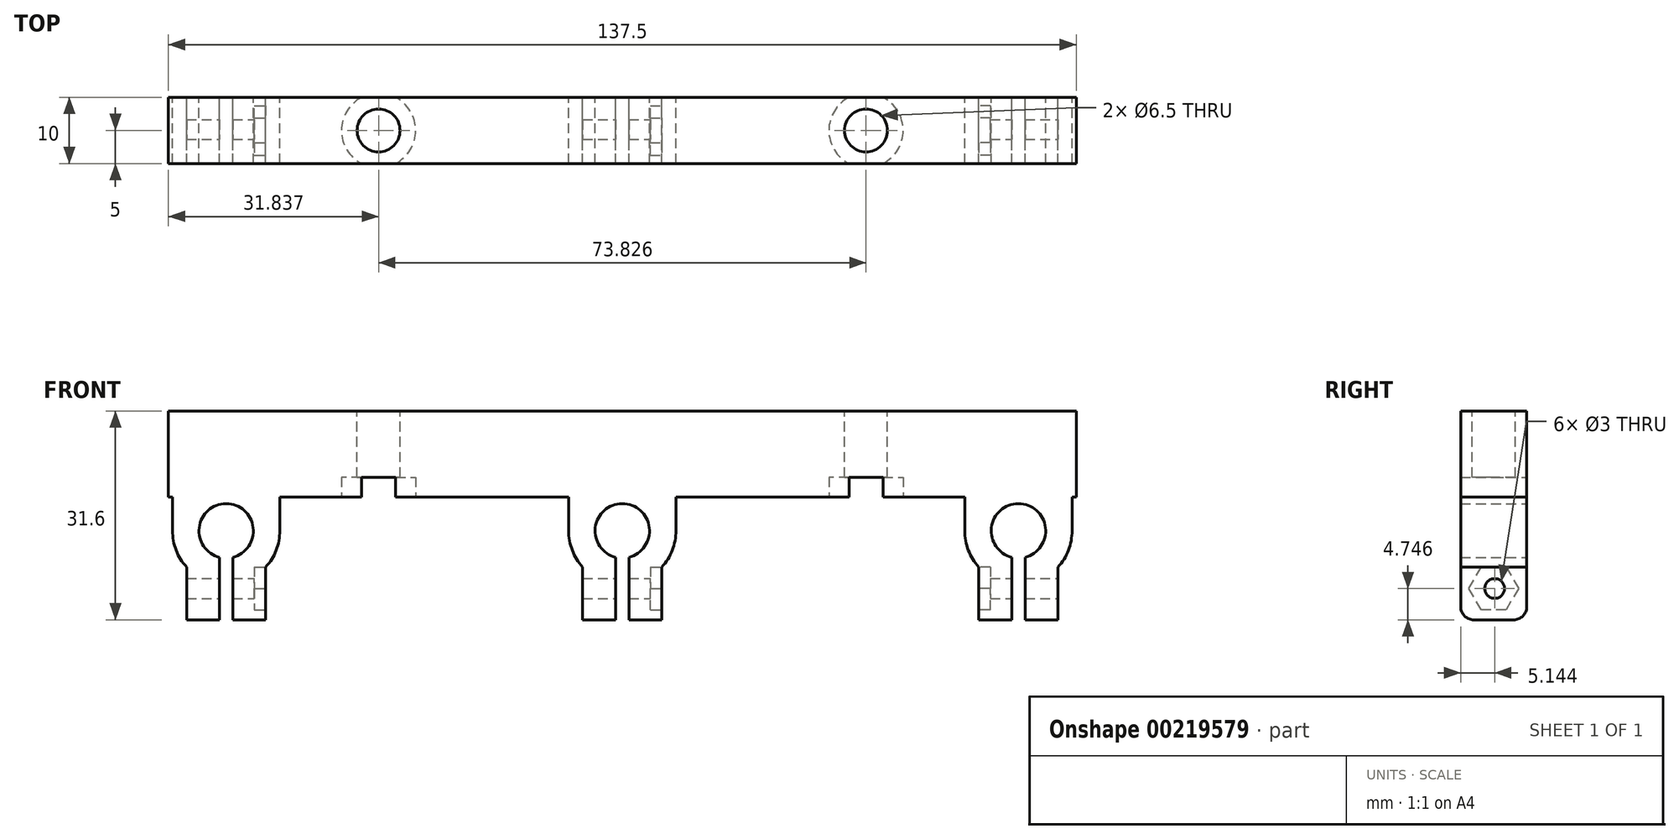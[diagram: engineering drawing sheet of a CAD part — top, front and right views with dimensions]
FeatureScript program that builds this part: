
annotation { "Feature Type Name" : "Feature", "Feature Type Description" : "" }
export const myFeature = defineFeature(function(context is Context, id is Id, definition is map)
    precondition{}
    {
        {
            var Q0;
            Q0=qCreatedBy(makeId("Top.planeOp"),FACE);
            var sketch = newSketch(context, id + "F0", { "sketchPlane" : qUnion([Q0])});
            skLineSegment(sketch, "E0.bottom", {"start": v(68.75, -5) * mm, "end": v(-68.75, -5) * mm});
            skLineSegment(sketch, "E0.top", {"start": v(68.75, 5) * mm, "end": v(-68.75, 5) * mm});
            skLineSegment(sketch, "E0.left", {"start": v(68.75, -5) * mm, "end": v(68.75, 5) * mm});
            skLineSegment(sketch, "E0.right", {"start": v(-68.75, -5) * mm, "end": v(-68.75, 5) * mm});
            skPoint(sketch, "E0.middle", {"position": v(0, 0) * mm});
            skSolve(sketch);
        }
        {
            var Q0;
            Q0 = qSketchRegion(id + "F0", true);
            extrude(context, id + "F1", {"entities" : qUnion([Q0]), "depth" : 9 * mm});
        }
        {
            var Q0;
            Q0=makeQuery(id+"F1.opExtrude","SWEPT_FACE",FACE,{"disambiguationData":[OSD([sQuery(id+"F0.wireOp",EDGE,"E0.top")])]});
            var sketch = newSketch(context, id + "F2", { "sketchPlane" : qUnion([Q0])});
            skCircle(sketch, "E1", {"center": v(0, -9.13) * mm, "radius": 4.12 * mm});
            skPoint(sketch, "E1.centerSnap0", {"position": v(0, 0) * mm});
            skCircle(sketch, "E2", {"center": v(-60, -9.12) * mm, "radius": 4.12 * mm});
            skCircle(sketch, "E3", {"center": v(60, -9.13) * mm, "radius": 4.12 * mm});
            skLineSegment(sketch, "E4", {"start": v(60, -9.13) * mm, "end": v(0, -9.13) * mm, "construction": true});
            skLineSegment(sketch, "E5", {"start": v(-60, -9.12) * mm, "end": v(0, -9.13) * mm, "construction": true});
            skArc(sketch, "E6", {"start": v(-68.12, -9.12) * mm, "mid": v(-60, -17.25) * mm, "end": v(-51.88, -9.12) * mm});
            skLineSegment(sketch, "E7", {"start": v(-68.12, -9.12) * mm, "end": v(-51.88, -9.12) * mm, "construction": true});
            skArc(sketch, "E8", {"start": v(-8.12, -9.13) * mm, "mid": v(0, -17.25) * mm, "end": v(8.12, -9.13) * mm});
            skLineSegment(sketch, "E9", {"start": v(-8.12, -9.12) * mm, "end": v(8.12, -9.13) * mm, "construction": true});
            skArc(sketch, "E10", {"start": v(51.88, -9.13) * mm, "mid": v(60, -17.25) * mm, "end": v(68.12, -9.13) * mm});
            skLineSegment(sketch, "E11", {"start": v(51.88, -9.13) * mm, "end": v(68.12, -9.13) * mm, "construction": true});
            skLineSegment(sketch, "E12", {"start": v(-68.12, -9.12) * mm, "end": v(-68.12, -4) * mm});
            skLineSegment(sketch, "E13", {"start": v(-51.88, -9.12) * mm, "end": v(-51.88, -4) * mm});
            skLineSegment(sketch, "E14", {"start": v(-8.12, -9.13) * mm, "end": v(-8.12, -4) * mm});
            skLineSegment(sketch, "E15", {"start": v(8.12, -9.13) * mm, "end": v(8.12, -4) * mm});
            skLineSegment(sketch, "E16", {"start": v(51.88, -9.13) * mm, "end": v(51.88, -4) * mm});
            skLineSegment(sketch, "E17", {"start": v(68.12, -9.13) * mm, "end": v(68.12, -4) * mm});
            skLineSegment(sketch, "E18", {"start": v(68.12, -4) * mm, "end": v(68.75, -4) * mm});
            skLineSegment(sketch, "E19", {"start": v(68.75, -4) * mm, "end": v(68.75, 0) * mm});
            skLineSegment(sketch, "E20", {"start": v(51.88, -4) * mm, "end": v(8.12, -4) * mm});
            skLineSegment(sketch, "E21", {"start": v(-8.12, -4) * mm, "end": v(-51.88, -4) * mm});
            skLineSegment(sketch, "E22", {"start": v(-68.12, -4) * mm, "end": v(-68.75, -4) * mm});
            skLineSegment(sketch, "E23", {"start": v(-68.75, -4) * mm, "end": v(-68.75, 0) * mm});
            skLineSegment(sketch, "E24.bottom", {"start": v(66, -14.6) * mm, "end": v(54, -14.6) * mm, "construction": true});
            skLineSegment(sketch, "E24.top", {"start": v(66, -22.6) * mm, "end": v(54, -22.6) * mm});
            skLineSegment(sketch, "E24.left", {"start": v(66, -14.6) * mm, "end": v(66, -22.6) * mm});
            skLineSegment(sketch, "E24.right", {"start": v(54, -14.6) * mm, "end": v(54, -22.6) * mm});
            skLineSegment(sketch, "E25.bottom", {"start": v(6, -14.6) * mm, "end": v(-6, -14.6) * mm, "construction": true});
            skLineSegment(sketch, "E25.top", {"start": v(6, -22.6) * mm, "end": v(-6, -22.6) * mm});
            skLineSegment(sketch, "E25.left", {"start": v(6, -14.6) * mm, "end": v(6, -22.6) * mm});
            skLineSegment(sketch, "E25.right", {"start": v(-6, -14.6) * mm, "end": v(-6, -22.6) * mm});
            skLineSegment(sketch, "E26.bottom", {"start": v(-54, -14.6) * mm, "end": v(-66, -14.6) * mm, "construction": true});
            skLineSegment(sketch, "E26.top", {"start": v(-54, -22.6) * mm, "end": v(-66, -22.6) * mm});
            skLineSegment(sketch, "E26.left", {"start": v(-54, -14.6) * mm, "end": v(-54, -22.6) * mm});
            skLineSegment(sketch, "E26.right", {"start": v(-66, -14.6) * mm, "end": v(-66, -22.6) * mm});
            skLineSegment(sketch, "E27.bottom", {"start": v(61, -13.13) * mm, "end": v(59, -13.13) * mm});
            skLineSegment(sketch, "E27.top", {"start": v(61, -22.6) * mm, "end": v(59, -22.6) * mm});
            skLineSegment(sketch, "E27.left", {"start": v(61, -13.13) * mm, "end": v(61, -22.6) * mm});
            skLineSegment(sketch, "E27.right", {"start": v(59, -13.13) * mm, "end": v(59, -22.6) * mm});
            skLineSegment(sketch, "E28.bottom", {"start": v(1, -13.13) * mm, "end": v(-1, -13.13) * mm});
            skLineSegment(sketch, "E28.top", {"start": v(1, -22.6) * mm, "end": v(-1, -22.6) * mm});
            skLineSegment(sketch, "E28.left", {"start": v(1, -13.13) * mm, "end": v(1, -22.6) * mm});
            skLineSegment(sketch, "E28.right", {"start": v(-1, -13.13) * mm, "end": v(-1, -22.6) * mm});
            skLineSegment(sketch, "E29.bottom", {"start": v(-59, -13.13) * mm, "end": v(-61, -13.13) * mm});
            skLineSegment(sketch, "E29.top", {"start": v(-59, -22.6) * mm, "end": v(-61, -22.6) * mm});
            skLineSegment(sketch, "E29.left", {"start": v(-59, -13.13) * mm, "end": v(-59, -22.6) * mm});
            skLineSegment(sketch, "E29.right", {"start": v(-61, -13.13) * mm, "end": v(-61, -22.6) * mm});
            skSolve(sketch);
        }
        {
            var Q0;
            {var subQ0=sQuery(id+"F2.wireOp",EDGE,"E26.right");Q0=makeQuery(id+"F2.imprint","IMPRINT",FACE,{"disambiguationData":[TD([[makeQuery(id+"F2.imprint","IMPRINT",EDGE,{"derivedFrom":subQ0}),1.0]])]});}
            var Q1;
            {var subQ0=sQuery(id+"F2.wireOp",EDGE,"E26.left");Q1=makeQuery(id+"F2.imprint","IMPRINT",FACE,{"disambiguationData":[TD([[makeQuery(id+"F2.imprint","IMPRINT",EDGE,{"derivedFrom":subQ0}),-1.0]])]});}
            var Q2;
            {var subQ0=sQuery(id+"F2.wireOp",EDGE,"E25.right");Q2=makeQuery(id+"F2.imprint","IMPRINT",FACE,{"disambiguationData":[TD([[makeQuery(id+"F2.imprint","IMPRINT",EDGE,{"derivedFrom":subQ0}),1.0]])]});}
            var Q3;
            {var subQ0=sQuery(id+"F2.wireOp",EDGE,"E25.left");Q3=makeQuery(id+"F2.imprint","IMPRINT",FACE,{"disambiguationData":[TD([[makeQuery(id+"F2.imprint","IMPRINT",EDGE,{"derivedFrom":subQ0}),-1.0]])]});}
            var Q4;
            {var subQ0=sQuery(id+"F2.wireOp",EDGE,"E24.right");Q4=makeQuery(id+"F2.imprint","IMPRINT",FACE,{"disambiguationData":[TD([[makeQuery(id+"F2.imprint","IMPRINT",EDGE,{"derivedFrom":subQ0}),1.0]])]});}
            var Q5;
            {var subQ0=sQuery(id+"F2.wireOp",EDGE,"E24.left");Q5=makeQuery(id+"F2.imprint","IMPRINT",FACE,{"disambiguationData":[TD([[makeQuery(id+"F2.imprint","IMPRINT",EDGE,{"derivedFrom":subQ0}),-1.0]])]});}
            var Q6;
            {var subQ3=sQuery(id+"F2.wireOp",EDGE,"E12");Q6=makeQuery(id+"F2.imprint","IMPRINT",FACE,{"disambiguationData":[TD([[makeQuery(id+"F2.imprint","IMPRINT",EDGE,{"derivedFrom":subQ3}),-1.0]])]});}
            var Q7;
            Q7=makeQuery(id+"F1.opExtrude","SWEPT_FACE",FACE,{"disambiguationData":[OSD([sQuery(id+"F0.wireOp",EDGE,"E0.bottom")])]});
            extrude(context, id + "F3", {"entities" : qUnion([Q0, Q1, Q2, Q3, Q4, Q5, Q6]), "operationType" : NewBodyOperationType.ADD, "endBound" : BoundingType.UP_TO_SURFACE, "oppositeDirection" : true, "endBoundEntityFace" : qUnion([Q7]), "depth" : 10 * mm});
        }
        {
            var Q0;
            Q0=makeQuery(id+"F3.opExtrude","SWEPT_FACE",FACE,{"disambiguationData":[OSD([sQuery(id+"F2.wireOp",EDGE,"E26.left")])]});
            var sketch = newSketch(context, id + "F4", { "sketchPlane" : qUnion([Q0])});
            skCircle(sketch, "E30.cCircle", {"center": v(0, -17.85) * mm, "radius": 3.25 * mm, "construction": true});
            skPoint(sketch, "E30.cCircle.centerSnap1", {"position": v(0, -14.6) * mm});
            skLineSegment(sketch, "E30.0", {"start": v(1.88, -14.6) * mm, "end": v(3.75, -17.85) * mm});
            skLineSegment(sketch, "E30.1", {"start": v(3.75, -17.85) * mm, "end": v(1.88, -21.1) * mm});
            skLineSegment(sketch, "E30.2", {"start": v(1.88, -21.1) * mm, "end": v(-1.88, -21.1) * mm});
            skLineSegment(sketch, "E30.3", {"start": v(-1.88, -21.1) * mm, "end": v(-3.75, -17.85) * mm});
            skLineSegment(sketch, "E30.4", {"start": v(-3.75, -17.85) * mm, "end": v(-1.88, -14.6) * mm});
            skLineSegment(sketch, "E30.5", {"start": v(-1.88, -14.6) * mm, "end": v(1.88, -14.6) * mm});
            skPoint(sketch, "E30.0.midPoint", {"position": v(2.81, -16.23) * mm});
            skLineSegment(sketch, "E31.0", {"start": v(5, -14.6) * mm, "end": v(-5, -14.6) * mm});
            skSolve(sketch);
        }
        {
            var Q0;
            Q0 = qSketchRegion(id + "F4", true);
            extrude(context, id + "F5", {"entities" : qUnion([Q0]), "operationType" : NewBodyOperationType.REMOVE, "oppositeDirection" : true, "depth" : 1.75 * mm});
        }
        {
            var Q0;
            Q0=makeQuery(id+"F3.opExtrude","SWEPT_FACE",FACE,{"disambiguationData":[OSD([sQuery(id+"F2.wireOp",EDGE,"E25.right")])]});
            var sketch = newSketch(context, id + "F6", { "sketchPlane" : qUnion([Q0])});
            skLineSegment(sketch, "E32.0.0", {"start": v(1.88, -14.6) * mm, "end": v(3.75, -17.85) * mm});
            skLineSegment(sketch, "E32.0.1", {"start": v(3.75, -17.85) * mm, "end": v(1.88, -21.1) * mm});
            skLineSegment(sketch, "E32.0.2", {"start": v(1.88, -21.1) * mm, "end": v(-1.88, -21.1) * mm});
            skLineSegment(sketch, "E32.0.3", {"start": v(-1.88, -21.1) * mm, "end": v(-3.75, -17.85) * mm});
            skLineSegment(sketch, "E32.0.4", {"start": v(-3.75, -17.85) * mm, "end": v(-1.88, -14.6) * mm});
            skLineSegment(sketch, "E32.0.5", {"start": v(-1.88, -14.6) * mm, "end": v(1.88, -14.6) * mm});
            skSolve(sketch);
        }
        {
            var Q0;
            Q0 = qSketchRegion(id + "F6", true);
            extrude(context, id + "F7", {"entities" : qUnion([Q0]), "operationType" : NewBodyOperationType.REMOVE, "oppositeDirection" : true, "depth" : 1.75 * mm});
        }
        {
            var Q0;
            Q0=makeQuery(id+"F3.opExtrude","SWEPT_FACE",FACE,{"disambiguationData":[OSD([sQuery(id+"F2.wireOp",EDGE,"E24.right")])]});
            var sketch = newSketch(context, id + "F8", { "sketchPlane" : qUnion([Q0])});
            skLineSegment(sketch, "E33.0.0", {"start": v(-1.88, -14.6) * mm, "end": v(-3.75, -17.85) * mm});
            skLineSegment(sketch, "E33.0.1", {"start": v(-3.75, -17.85) * mm, "end": v(-1.88, -21.1) * mm});
            skLineSegment(sketch, "E33.0.2", {"start": v(-1.88, -21.1) * mm, "end": v(1.88, -21.1) * mm});
            skLineSegment(sketch, "E33.0.3", {"start": v(1.88, -21.1) * mm, "end": v(3.75, -17.85) * mm});
            skLineSegment(sketch, "E33.0.4", {"start": v(3.75, -17.85) * mm, "end": v(1.88, -14.6) * mm});
            skLineSegment(sketch, "E33.0.5", {"start": v(1.88, -14.6) * mm, "end": v(-1.88, -14.6) * mm});
            skSolve(sketch);
        }
        {
            var Q0;
            Q0 = qSketchRegion(id + "F8", true);
            extrude(context, id + "F9", {"entities" : qUnion([Q0]), "operationType" : NewBodyOperationType.REMOVE, "oppositeDirection" : true, "depth" : 1.75 * mm});
        }
        {
            var Q0;
            Q0=makeQuery(id+"F3.opExtrude","SWEPT_FACE",FACE,{"disambiguationData":[OSD([sQuery(id+"F2.wireOp",EDGE,"E26.right")])]});
            var sketch = newSketch(context, id + "F10", { "sketchPlane" : qUnion([Q0])});
            skCircle(sketch, "E34", {"center": v(0.14, -17.85) * mm, "radius": 1.5 * mm});
            skPoint(sketch, "E34.centerSnap0", {"position": v(-3.75, -17.85) * mm});
            skSolve(sketch);
        }
        {
            var Q0;
            Q0 = qSketchRegion(id + "F10", true);
            extrude(context, id + "F11", {"entities" : qUnion([Q0]), "operationType" : NewBodyOperationType.REMOVE, "endBound" : BoundingType.THROUGH_ALL, "oppositeDirection" : true, "depth" : 25 * mm});
        }
        {
            var Q0;
            Q0=makeQuery(id+"F1.opExtrude","CAP_FACE",FACE,{"disambiguationData":[OSD([sQuery(id+"F0.wireOp",EDGE,"E0.bottom"),sQuery(id+"F0.wireOp",EDGE,"E0.top"),sQuery(id+"F0.wireOp",EDGE,"E0.left"),sQuery(id+"F0.wireOp",EDGE,"E0.right")])],"isStart":false});
            var sketch = newSketch(context, id + "F12", { "sketchPlane" : qUnion([Q0])});
            skCircle(sketch, "E35", {"center": v(36.91, 0) * mm, "radius": 3.25 * mm});
            skLineSegment(sketch, "E36", {"start": v(0, 0) * mm, "end": v(36.91, 0) * mm, "construction": true});
            skCircle(sketch, "E37", {"center": v(-36.91, 0) * mm, "radius": 3.25 * mm});
            skLineSegment(sketch, "E38", {"start": v(0, 0) * mm, "end": v(-36.91, 0) * mm, "construction": true});
            skSolve(sketch);
        }
        {
            var Q0;
            Q0 = qSketchRegion(id + "F12", true);
            extrude(context, id + "F13", {"entities" : qUnion([Q0]), "operationType" : NewBodyOperationType.REMOVE, "endBound" : BoundingType.THROUGH_ALL, "oppositeDirection" : true, "depth" : 25 * mm});
        }
        {
            var Q0;
            Q0=makeQuery(id+"F3.opExtrude","SWEPT_FACE",FACE,{"disambiguationData":[OSD([sQuery(id+"F2.wireOp",EDGE,"E26.right")])]});
            var sketch = newSketch(context, id + "F14", { "sketchPlane" : qUnion([Q0])});
            skArc(sketch, "E39", {"start": v(-5, -20.6) * mm, "mid": v(-4.41, -22.02) * mm, "end": v(-3, -22.6) * mm});
            skArc(sketch, "E40", {"start": v(3, -22.6) * mm, "mid": v(4.41, -22.02) * mm, "end": v(5, -20.6) * mm});
            skSolve(sketch);
        }
        {
            var Q0;
            Q0 = qSketchRegion(id + "F14", true);
            var Q1;
            {var subQ0=sQuery(id+"F14.wireOp",EDGE,"E39");Q1=makeQuery(id+"F14.imprint","IMPRINT",FACE,{"disambiguationData":[TD([[makeQuery(id+"F14.imprint","IMPRINT",EDGE,{"derivedFrom":subQ0}),-1.0]])]});}
            var Q2;
            {var subQ0=sQuery(id+"F14.wireOp",EDGE,"E40");Q2=makeQuery(id+"F14.imprint","IMPRINT",FACE,{"disambiguationData":[TD([[makeQuery(id+"F14.imprint","IMPRINT",EDGE,{"derivedFrom":subQ0}),-1.0]])]});}
            extrude(context, id + "F15", {"entities" : qUnion([Q0, Q1, Q2]), "operationType" : NewBodyOperationType.REMOVE, "endBound" : BoundingType.THROUGH_ALL, "oppositeDirection" : true, "depth" : 25 * mm});
        }
        {
            var Q0;
            Q0=makeQuery(id+"F3.opExtrude","SWEPT_FACE",FACE,{"disambiguationData":[OSD([sQuery(id+"F2.wireOp",EDGE,"E21")])]});
            var sketch = newSketch(context, id + "F16", { "sketchPlane" : qUnion([Q0])});
            skCircle(sketch, "E41.0", {"center": v(36.91, 0) * mm, "radius": 3.25 * mm});
            skCircle(sketch, "E41.1", {"center": v(-36.91, 0) * mm, "radius": 3.25 * mm});
            skCircle(sketch, "E42", {"center": v(-36.91, 0) * mm, "radius": 5.62 * mm});
            skCircle(sketch, "E43", {"center": v(36.91, 0) * mm, "radius": 5.62 * mm});
            skSolve(sketch);
        }
        {
            var Q0;
            Q0 = qSketchRegion(id + "F16", true);
            extrude(context, id + "F17", {"entities" : qUnion([Q0]), "operationType" : NewBodyOperationType.REMOVE, "oppositeDirection" : true, "depth" : 3 * mm});
        }
    });
